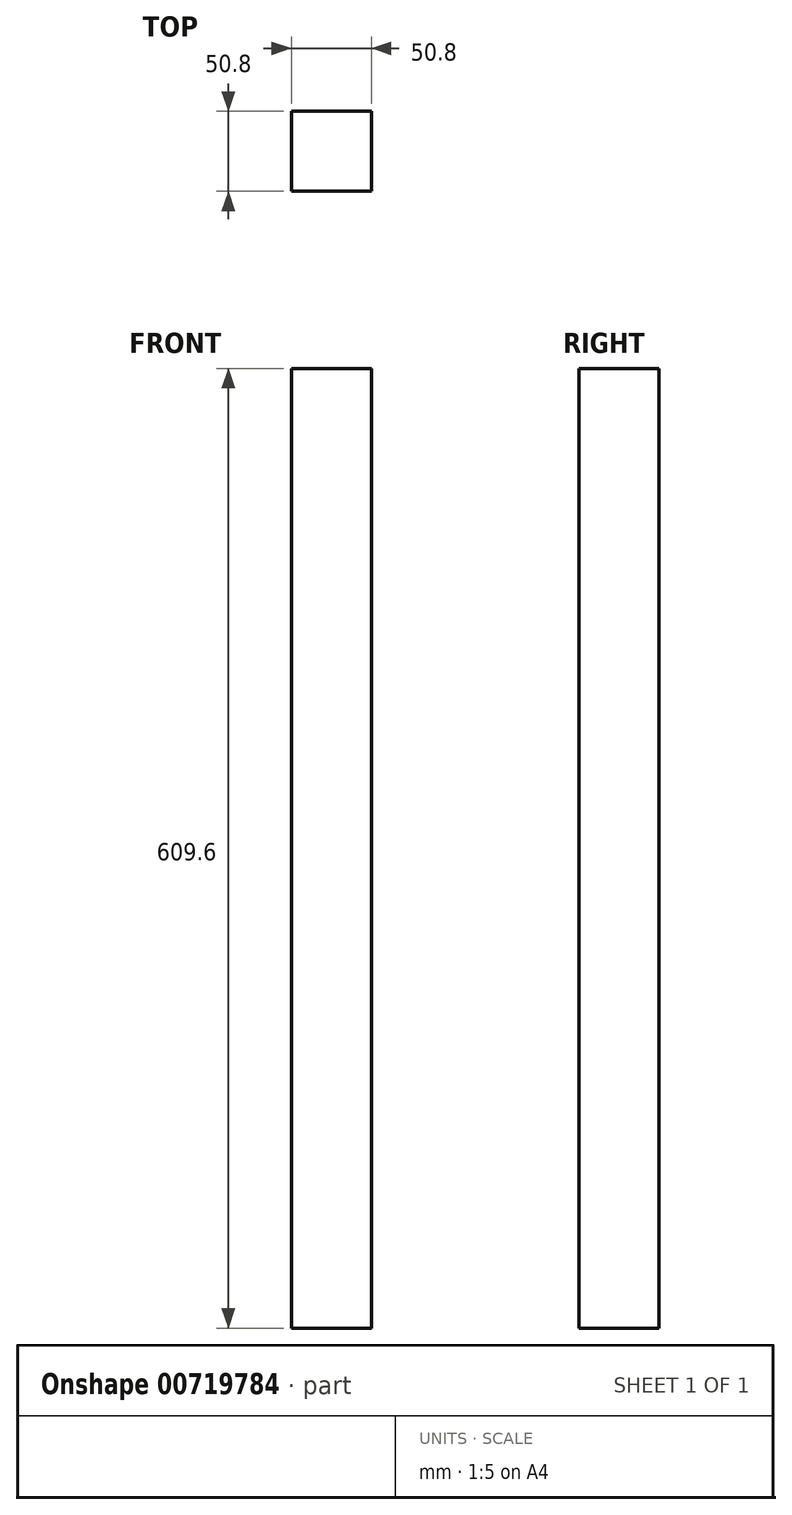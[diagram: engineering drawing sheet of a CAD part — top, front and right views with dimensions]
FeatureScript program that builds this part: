
annotation { "Feature Type Name" : "Feature", "Feature Type Description" : "" }
export const myFeature = defineFeature(function(context is Context, id is Id, definition is map)
    precondition{}
    {
        {
            var Q0;
            Q0=qCreatedBy(makeId("Top.planeOp"),FACE);
            var sketch = newSketch(context, id + "F0", { "sketchPlane" : qUnion([Q0])});
            skLineSegment(sketch, "E0.bottom", {"start": v(-75.23, -75.18) * mm, "end": v(-24.43, -75.18) * mm});
            skLineSegment(sketch, "E0.top", {"start": v(-75.23, -24.38) * mm, "end": v(-24.43, -24.38) * mm});
            skLineSegment(sketch, "E0.left", {"start": v(-75.23, -75.18) * mm, "end": v(-75.23, -24.38) * mm});
            skLineSegment(sketch, "E0.right", {"start": v(-24.43, -75.18) * mm, "end": v(-24.43, -24.38) * mm});
            skSolve(sketch);
        }
        {
            var Q0;
            Q0 = qSketchRegion(id + "F0", true);
            extrude(context, id + "F1", {"entities" : qUnion([Q0]), "depth" : 609.6 * mm, "offsetDistance" : 25.4 * mm});
        }
    });
